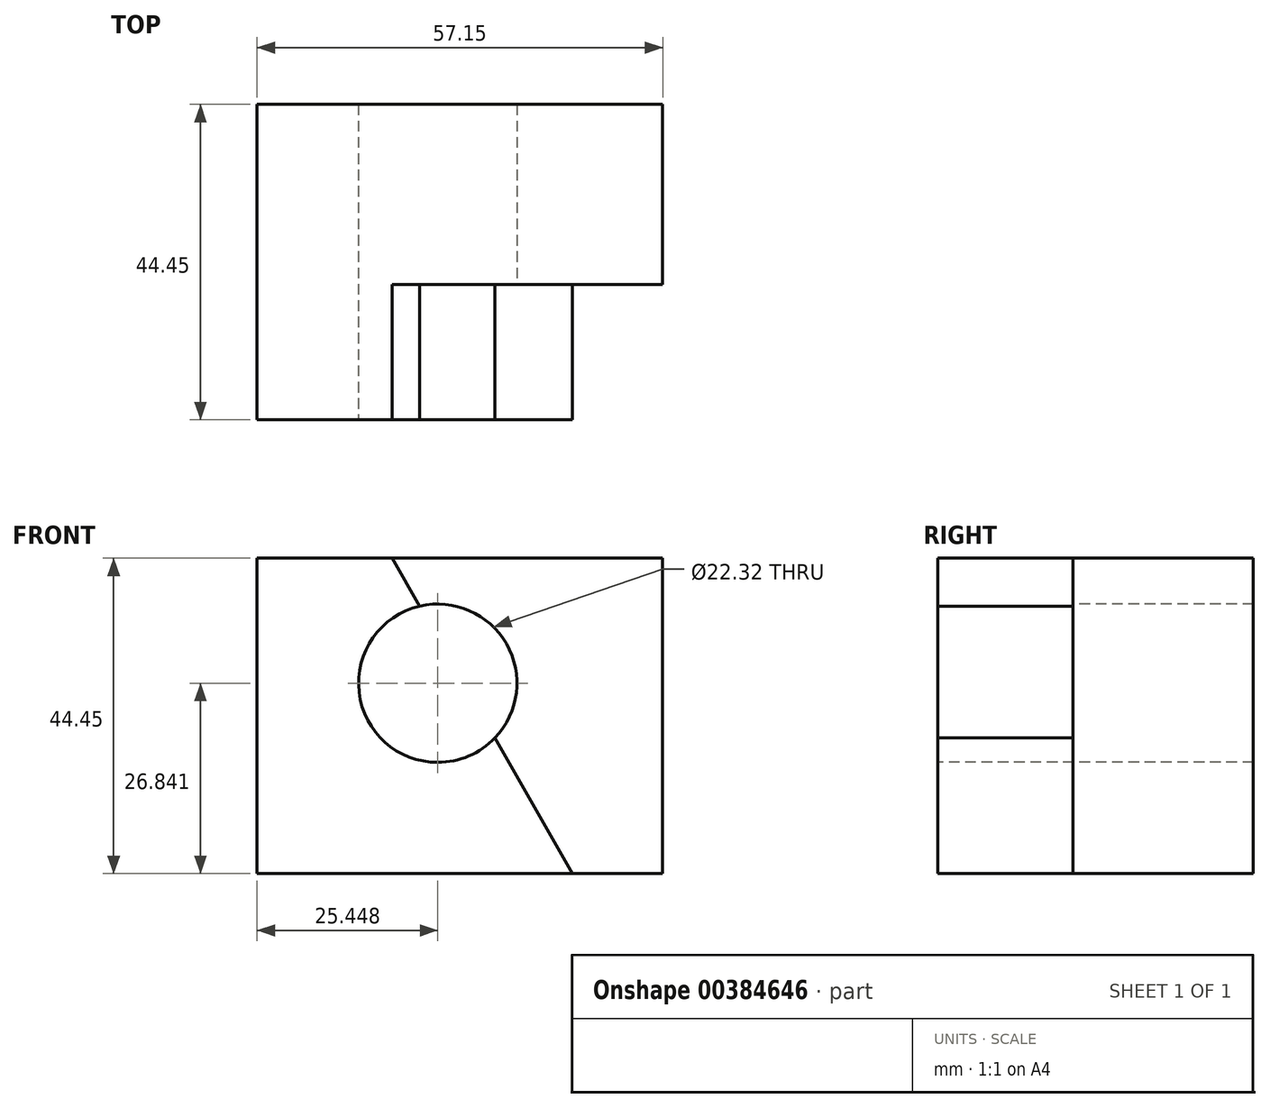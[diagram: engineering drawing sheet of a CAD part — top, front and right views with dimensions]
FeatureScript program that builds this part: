
annotation { "Feature Type Name" : "Feature", "Feature Type Description" : "" }
export const myFeature = defineFeature(function(context is Context, id is Id, definition is map)
    precondition{}
    {
        {
            var Q0;
            Q0=qCreatedBy(makeId("Front.planeOp"),FACE);
            var sketch = newSketch(context, id + "F0", { "sketchPlane" : qUnion([Q0])});
            skLineSegment(sketch, "E0", {"start": v(-20.5, 0) * mm, "end": v(-20.5, 44.45) * mm});
            skLineSegment(sketch, "E1", {"start": v(-20.5, 44.45) * mm, "end": v(36.66, 44.45) * mm});
            skLineSegment(sketch, "E2", {"start": v(36.66, 44.45) * mm, "end": v(36.66, 0) * mm});
            skLineSegment(sketch, "E3", {"start": v(36.66, 0) * mm, "end": v(-20.5, 0) * mm});
            skSolve(sketch);
        }
        {
            var Q0;
            Q0 = qSketchRegion(id + "F0", true);
            extrude(context, id + "F1", {"entities" : qUnion([Q0]), "depth" : 25.4 * mm});
        }
        {
            var Q0;
            Q0=makeQuery(id+"F1.opExtrude","CAP_FACE",FACE,{"disambiguationData":[OSD([sQuery(id+"F0.wireOp",EDGE,"E0"),sQuery(id+"F0.wireOp",EDGE,"E1"),sQuery(id+"F0.wireOp",EDGE,"E2"),sQuery(id+"F0.wireOp",EDGE,"E3")])],"isStart":false});
            var sketch = newSketch(context, id + "F2", { "sketchPlane" : qUnion([Q0])});
            skLineSegment(sketch, "E4", {"start": v(-20.5, 0) * mm, "end": v(-20.5, 44.45) * mm});
            skLineSegment(sketch, "E5", {"start": v(-20.5, 44.45) * mm, "end": v(-1.44, 44.45) * mm});
            skLineSegment(sketch, "E6", {"start": v(-1.44, 44.45) * mm, "end": v(23.96, 0) * mm});
            skLineSegment(sketch, "E7", {"start": v(23.96, 0) * mm, "end": v(-20.5, 0) * mm});
            skSolve(sketch);
        }
        {
            var Q0;
            Q0=makeQuery(id+"F2.imprint","IMPRINT",FACE,{"disambiguationData":[TD([[makeQuery(id+"F2.imprint","IMPRINT",EDGE,{"derivedFrom":sQuery(id+"F2.wireOp",EDGE,"E4")}),-1.0]])]});
            extrude(context, id + "F3", {"entities" : qUnion([Q0]), "operationType" : NewBodyOperationType.ADD, "depth" : 19.05 * mm});
        }
        {
            var Q0;
            Q0=makeQuery(id+"F3.opExtrude","CAP_FACE",FACE,{"disambiguationData":[OSD([sQuery(id+"F2.wireOp",EDGE,"E4"),sQuery(id+"F2.wireOp",EDGE,"E5"),sQuery(id+"F2.wireOp",EDGE,"E6"),sQuery(id+"F2.wireOp",EDGE,"E7")])],"isStart":false});
            var sketch = newSketch(context, id + "F4", { "sketchPlane" : qUnion([Q0])});
            skCircle(sketch, "E8", {"center": v(4.96, 26.84) * mm, "radius": 11.16 * mm});
            skSolve(sketch);
        }
        {
            var Q0;
            {var subQ0=sQuery(id+"F4.wireOp",EDGE,"E8");var subQ1=makeQuery(id+"F3.opExtrude","CAP_EDGE",EDGE,{"disambiguationData":[OSD([sQuery(id+"F2.wireOp",EDGE,"E6")])],"isStart":false});var subQ2=makeQuery(id+"F4.imprint","INTERSECT",VERTEX,{"disambiguationData":[OD(0.0)],"derivedFrom":[subQ1,subQ0]});Q0=makeQuery(id+"F4.imprint","IMPRINT",FACE,{"disambiguationData":[TD([[makeQuery(id+"F4.imprint","IMPRINT",EDGE,{"disambiguationData":[TD([[subQ2,-1.0]])],"derivedFrom":subQ0}),1.0]])]});}
            var Q1;
            {var subQ0=sQuery(id+"F4.wireOp",EDGE,"E8");var subQ1=makeQuery(id+"F3.opExtrude","CAP_EDGE",EDGE,{"disambiguationData":[OSD([sQuery(id+"F2.wireOp",EDGE,"E6")])],"isStart":false});var subQ2=makeQuery(id+"F4.imprint","INTERSECT",VERTEX,{"disambiguationData":[OD(0.0)],"derivedFrom":[subQ1,subQ0]});Q1=makeQuery(id+"F4.imprint","IMPRINT",FACE,{"disambiguationData":[TD([[makeQuery(id+"F4.imprint","IMPRINT",EDGE,{"disambiguationData":[TD([[subQ2,1.0]])],"derivedFrom":subQ0}),1.0]])]});}
            extrude(context, id + "F5", {"entities" : qUnion([Q0, Q1]), "operationType" : NewBodyOperationType.REMOVE, "oppositeDirection" : true, "depth" : 50.8 * mm});
        }
    });
